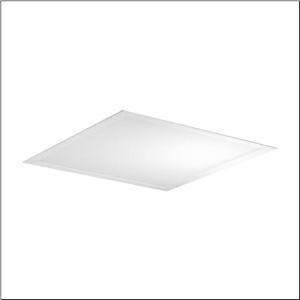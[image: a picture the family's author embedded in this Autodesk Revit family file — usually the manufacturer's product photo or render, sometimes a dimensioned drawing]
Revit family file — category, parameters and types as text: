
# Revit family: apollon_r__31_square_51mp11wd2n42_7747
name_source: partatom
category: Lighting Fixtures
units: mm (PartAtom-declared; Revit-internal decimal feet)

## family parameters
Cut with Voids When Loaded = No
Host = Face
Light Source = No
Part Type = Normal
Room Calculation Point = No
Round Connector Dimension = Use Diameter
Shared = No

## types (1)
- --- (1 x LED, 4000 lm, 27.5 W, 5000K)
    Apparent Load = 28 VA
    CIE Flux Codes = 62 87 97 100 100
    Color Rendering = 80
    Color Temperature = 5000K
    Default Elevation = 1800 mm
    Description = Apollon® 31 square, office luminaire, primary optical cover: micro prismatic cover, of PMMA, CAT 2 (L<= 3000cd/m²), light emission: direct distribution, primary light characteristic: symmetric, installation type: lay-in mounting, LED, rated luminous flux: 4.000lm, luminous efficacy: 145lm/W, light colour: 840/850, colour temperature: 4000/5000K, with terminal, 5-pole, mains connection: 220..240V, AC/DC, 0/50..60Hz, rated input power: 28W, housing, of aluminium, traffic white (RAL 9016), module: M625, length: 620mm, width: 620mm, height: 32mm, housing upper side, of sheet steel, galvanised, protection rating (complete): IP20, protection rating (on room side): IP40, insulation class (complete): insulation class II (safety insulation), certification: CE, ENEC, impact resistance: IK03, permissible operating ambient temperature: -20..+40°C, permissible storage temperature: -20..+60°C, packaging unit: 1 piece
    Height = 0 mm  [stored 0 ft]
    Lamp = 1 x LED
    Lamp Light Flux = 4000 lm
    Lamp Power = 27.5 W
    Lamp count = 1
    Length = 620 mm
    Luminous efficacy = 145 lm/W
    Manufacturer = Siteco
    ModVariant = No
    Model = 51MP11WD2N42
    Mounting Place = Ceiling
    Mounting Type = Recessed
    Number of Poles = 1
    OnlyDefault = Yes
    Power Factor = 1
    Product Name = Apollon® 31 square
    Product group = office luminaire | ceiling recessed
    ProductGroupID = 401
    Protection Class = Protection class II
    Protection Degree = IP 20
    RLX_Detail_Level = 1
    RLX_Emergency_Light_Flux = 0 lm
    RLX_Emergency_Type = 0
    RLX_Emergency_Type_DB = No
    RlxData = <blob elided: 13161 chars, md5=46cd47f6>
    Socket = socket
    Standby Power = 0 W
    System Light Flux = 4000 lm
    System Power = 28 W
    Type Comments = individual setting: colour temperature 5000K
    Type Image = l_1291039.jpg
    URL = http://relux.com
    VarID = @adj_027789
    Voltage = 0 V
    Weight = 0.00 kg
    Width = 620 mm

note: [stored X ft] marks values corroborated as IEEE doubles in the binary element streams (Revit-internal decimal feet)

## geometry (parser evidence)
native form markers: Sweep x10
no freeform markers — native parametric forms only
